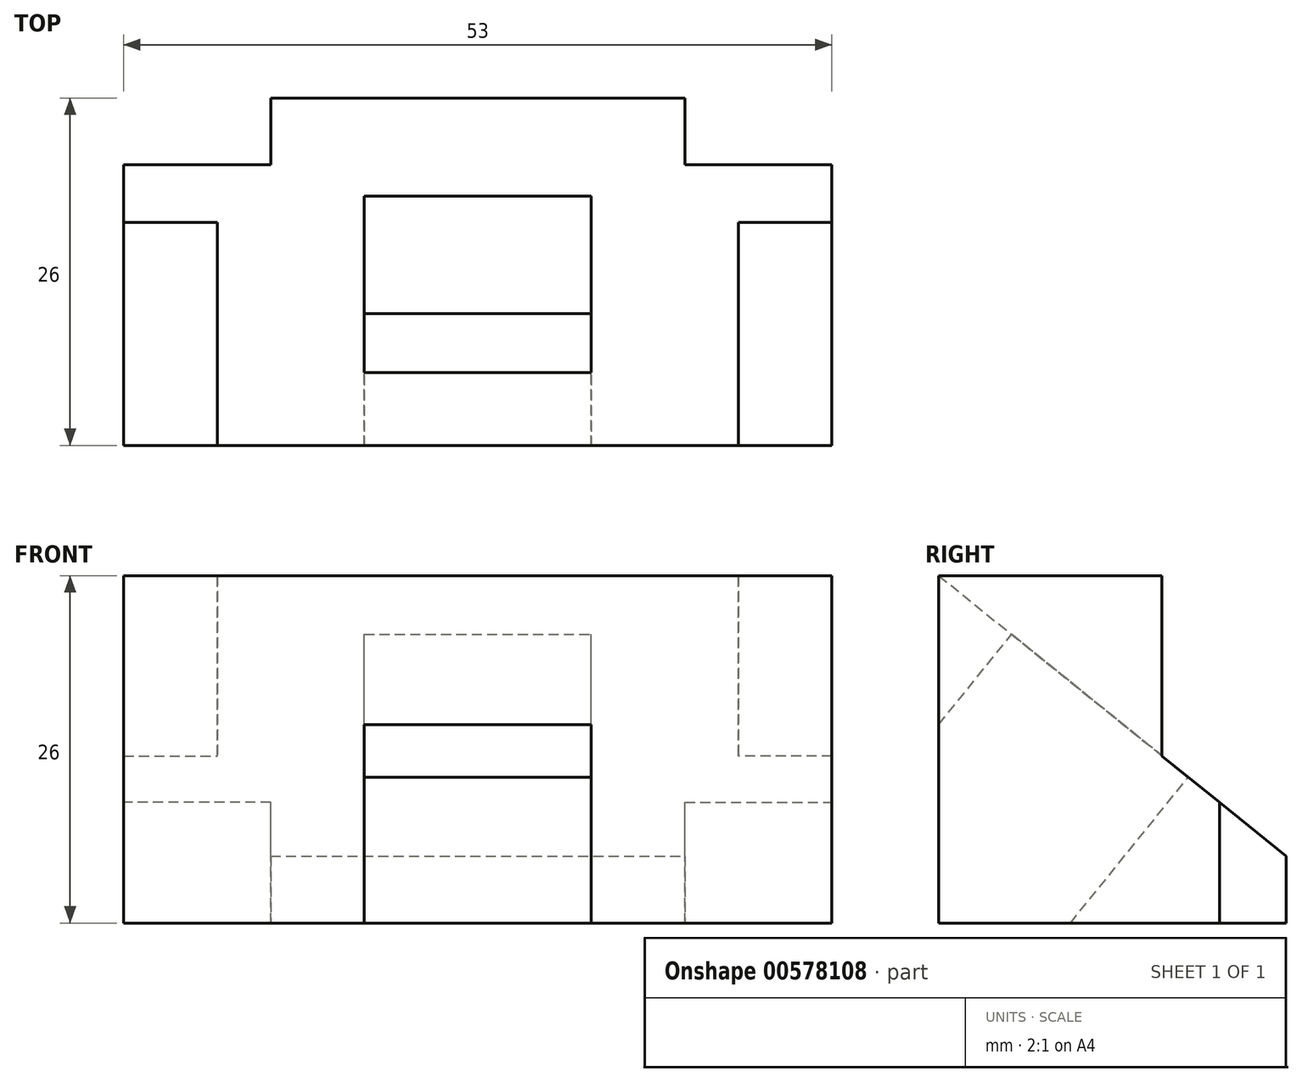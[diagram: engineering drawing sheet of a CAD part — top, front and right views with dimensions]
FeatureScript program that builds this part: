
annotation { "Feature Type Name" : "Feature", "Feature Type Description" : "" }
export const myFeature = defineFeature(function(context is Context, id is Id, definition is map)
    precondition{}
    {
        {
            var Q0;
            Q0=qCreatedBy(makeId("Top.planeOp"),FACE);
            var sketch = newSketch(context, id + "F0", { "sketchPlane" : qUnion([Q0])});
            skLineSegment(sketch, "E0.bottom", {"start": v(0, 0) * mm, "end": v(53, 0) * mm});
            skLineSegment(sketch, "E0.top", {"start": v(0, 26) * mm, "end": v(53, 26) * mm});
            skLineSegment(sketch, "E0.left", {"start": v(0, 0) * mm, "end": v(0, 26) * mm});
            skLineSegment(sketch, "E0.right", {"start": v(53, 0) * mm, "end": v(53, 26) * mm});
            skSolve(sketch);
        }
        {
            var Q0;
            Q0=makeQuery(id+"F0.imprint","IMPRINT",FACE,{"disambiguationData":[TD([[makeQuery(id+"F0.imprint","IMPRINT",EDGE,{"derivedFrom":sQuery(id+"F0.wireOp",EDGE,"E0.bottom")}),1.0]])]});
            extrude(context, id + "F1", {"entities" : qUnion([Q0]), "depth" : 26 * mm, "offsetDistance" : 25 * mm});
        }
        {
            var Q0;
            Q0=makeQuery(id+"F1.opExtrude","SWEPT_FACE",FACE,{"disambiguationData":[OSD([sQuery(id+"F0.wireOp",EDGE,"E0.right")])]});
            cPlane(context, id + "F2", {"entities" : qUnion([Q0]), "cplaneType" : CPlaneType.OFFSET, "offset" : 7 * mm, "oppositeDirection" : true, "width" : 150 * mm, "height" : 150 * mm});
        }
        {
            var Q0;
            Q0=qCreatedBy(id+"F2.planeOp",FACE);
            var sketch = newSketch(context, id + "F3", { "sketchPlane" : qUnion([Q0])});
            skLineSegment(sketch, "E1", {"start": v(0, 26) * mm, "end": v(26, 5) * mm});
            skLineSegment(sketch, "E2", {"start": v(26, 5) * mm, "end": v(26, 26) * mm});
            skLineSegment(sketch, "E3", {"start": v(26, 26) * mm, "end": v(0, 26) * mm});
            skSolve(sketch);
        }
        {
            var Q0;
            Q0 = qSketchRegion(id + "F3", true);
            extrude(context, id + "F4", {"entities" : qUnion([Q0]), "operationType" : NewBodyOperationType.REMOVE, "oppositeDirection" : true, "depth" : 39 * mm, "offsetDistance" : 25 * mm});
        }
        {
            var Q0;
            Q0=makeQuery(id+"F1.opExtrude","SWEPT_FACE",FACE,{"disambiguationData":[OSD([sQuery(id+"F0.wireOp",EDGE,"E0.right")])]});
            var sketch = newSketch(context, id + "F5", { "sketchPlane" : qUnion([Q0])});
            skLineSegment(sketch, "E4.bottom", {"start": v(26, 0) * mm, "end": v(21, 0) * mm});
            skLineSegment(sketch, "E4.top", {"start": v(26, 11) * mm, "end": v(21, 11) * mm});
            skLineSegment(sketch, "E4.left", {"start": v(26, 0) * mm, "end": v(26, 11) * mm});
            skLineSegment(sketch, "E4.right", {"start": v(21, 0) * mm, "end": v(21, 11) * mm});
            skSolve(sketch);
        }
        {
            var Q0;
            Q0 = qSketchRegion(id + "F5", true);
            extrude(context, id + "F6", {"entities" : qUnion([Q0]), "operationType" : NewBodyOperationType.REMOVE, "oppositeDirection" : true, "depth" : 11 * mm, "offsetDistance" : 25 * mm});
        }
        {
            var Q0;
            Q0=makeQuery(id+"F1.opExtrude","SWEPT_FACE",FACE,{"disambiguationData":[OSD([sQuery(id+"F0.wireOp",EDGE,"E0.right")])]});
            var sketch = newSketch(context, id + "F7", { "sketchPlane" : qUnion([Q0])});
            skLineSegment(sketch, "E5", {"start": v(16.7, 14) * mm, "end": v(16.7, 26) * mm});
            skLineSegment(sketch, "E6", {"start": v(16.7, 14) * mm, "end": v(25.18, 10.04) * mm});
            skSolve(sketch);
        }
        {
            var Q0;
            Q0 = qSketchRegion(id + "F7", true);
            var Q1;
            {var subQ3=sQuery(id+"F7.wireOp",EDGE,"E5");Q1=makeQuery(id+"F7.imprint","IMPRINT",FACE,{"disambiguationData":[TD([[makeQuery(id+"F7.imprint","IMPRINT",EDGE,{"derivedFrom":subQ3}),-1.0]])]});}
            extrude(context, id + "F8", {"entities" : qUnion([Q0, Q1]), "operationType" : NewBodyOperationType.REMOVE, "endBound" : BoundingType.THROUGH_ALL, "oppositeDirection" : true, "depth" : 25 * mm, "offsetDistance" : 25 * mm});
        }
        {
            var Q0;
            Q0=makeQuery(id+"F1.opExtrude","SWEPT_FACE",FACE,{"disambiguationData":[OSD([sQuery(id+"F0.wireOp",EDGE,"E0.right")])]});
            var sketch = newSketch(context, id + "F9", { "sketchPlane" : qUnion([Q0])});
            skLineSegment(sketch, "E7", {"start": v(21, 11) * mm, "end": v(21, 12) * mm});
            skSolve(sketch);
        }
        {
            var Q0;
            {var subQ0=sQuery(id+"F9.wireOp",EDGE,"E7");Q0=makeQuery(id+"F9.imprint","IMPRINT",FACE,{"disambiguationData":[TD([[makeQuery(id+"F9.imprint","IMPRINT",EDGE,{"derivedFrom":subQ0}),-1.0]])]});}
            extrude(context, id + "F10", {"entities" : qUnion([Q0]), "operationType" : NewBodyOperationType.REMOVE, "oppositeDirection" : true, "depth" : 18 * mm, "offsetDistance" : 25 * mm});
        }
        {
            var Q0;
            Q0=makeQuery(id+"F1.opExtrude","SWEPT_FACE",FACE,{"disambiguationData":[OSD([sQuery(id+"F0.wireOp",EDGE,"E0.right")])]});
            var sketch = newSketch(context, id + "F11", { "sketchPlane" : qUnion([Q0])});
            skLineSegment(sketch, "E8", {"start": v(21, 9.04) * mm, "end": v(16.7, 14) * mm});
            skSolve(sketch);
        }
        {
            var Q0;
            {var subQ0=sQuery(id+"F11.wireOp",EDGE,"E8");Q0=makeQuery(id+"F11.imprint","IMPRINT",FACE,{"disambiguationData":[TD([[makeQuery(id+"F11.imprint","IMPRINT",EDGE,{"derivedFrom":subQ0}),-1.0]])]});}
            extrude(context, id + "F12", {"entities" : qUnion([Q0]), "operationType" : NewBodyOperationType.REMOVE, "endBound" : BoundingType.THROUGH_ALL, "oppositeDirection" : true, "depth" : 25 * mm, "offsetDistance" : 25 * mm});
        }
        {
            var Q0;
            Q0=makeQuery(id+"F4.boolean.opBoolean","COPY",FACE,{"derivedFrom":makeQuery(id+"F4.opExtrude","CAP_FACE",FACE,{"disambiguationData":[OSD([sQuery(id+"F3.wireOp",EDGE,"E1"),sQuery(id+"F3.wireOp",EDGE,"E2"),sQuery(id+"F3.wireOp",EDGE,"E3")])],"isStart":true})});
            var sketch = newSketch(context, id + "F13", { "sketchPlane" : qUnion([Q0])});
            skLineSegment(sketch, "E9", {"start": v(-16.7, 14) * mm, "end": v(-16.7, 12.51) * mm});
            skSolve(sketch);
        }
        {
            var Q0;
            Q0 = qSketchRegion(id + "F13", true);
            var Q1;
            {var subQ0=sQuery(id+"F13.wireOp",EDGE,"E9");Q1=makeQuery(id+"F13.imprint","IMPRINT",FACE,{"disambiguationData":[TD([[makeQuery(id+"F13.imprint","IMPRINT",EDGE,{"derivedFrom":subQ0}),-1.0]])]});}
            extrude(context, id + "F14", {"entities" : qUnion([Q0, Q1]), "operationType" : NewBodyOperationType.REMOVE, "oppositeDirection" : true, "depth" : 25 * mm, "offsetDistance" : 25 * mm});
        }
        {
            var Q0;
            Q0=makeQuery(id+"F1.opExtrude","SWEPT_FACE",FACE,{"disambiguationData":[OSD([sQuery(id+"F0.wireOp",EDGE,"E0.left")])]});
            var sketch = newSketch(context, id + "F15", { "sketchPlane" : qUnion([Q0])});
            skLineSegment(sketch, "E10", {"start": v(-26, 5.5) * mm, "end": v(-21, 9.04) * mm});
            skLineSegment(sketch, "E11", {"start": v(-21, 9.04) * mm, "end": v(-21, 0) * mm});
            skLineSegment(sketch, "E12", {"start": v(-21, 0) * mm, "end": v(-26, 0) * mm});
            skLineSegment(sketch, "E13", {"start": v(-26, 0) * mm, "end": v(-26, 5.5) * mm});
            skSolve(sketch);
        }
        {
            var Q0;
            {var subQ4=sQuery(id+"F15.wireOp",EDGE,"E10");Q0=makeQuery(id+"F15.imprint","IMPRINT",FACE,{"disambiguationData":[TD([[makeQuery(id+"F15.imprint","IMPRINT",EDGE,{"derivedFrom":subQ4}),1.0]])]});}
            extrude(context, id + "F16", {"entities" : qUnion([Q0]), "operationType" : NewBodyOperationType.REMOVE, "oppositeDirection" : true, "depth" : 25 * mm, "offsetDistance" : 25 * mm});
        }
        {
            var Q0;
            Q0=makeQuery(id+"F4.boolean.opBoolean","COPY",FACE,{"derivedFrom":makeQuery(id+"F4.opExtrude","CAP_FACE",FACE,{"disambiguationData":[OSD([sQuery(id+"F3.wireOp",EDGE,"E1"),sQuery(id+"F3.wireOp",EDGE,"E2"),sQuery(id+"F3.wireOp",EDGE,"E3")])],"isStart":false})});
            var sketch = newSketch(context, id + "F17", { "sketchPlane" : qUnion([Q0])});
            skLineSegment(sketch, "E14", {"start": v(16.7, 14) * mm, "end": v(16.7, 12.51) * mm});
            skSolve(sketch);
        }
        {
            var Q0;
            Q0 = qSketchRegion(id + "F17", true);
            var Q1;
            {var subQ4=sQuery(id+"F17.wireOp",EDGE,"E14");Q1=makeQuery(id+"F17.imprint","IMPRINT",FACE,{"disambiguationData":[TD([[makeQuery(id+"F17.imprint","IMPRINT",EDGE,{"derivedFrom":subQ4}),1.0]])]});}
            extrude(context, id + "F18", {"entities" : qUnion([Q0, Q1]), "operationType" : NewBodyOperationType.REMOVE, "endBound" : BoundingType.THROUGH_ALL, "oppositeDirection" : true, "depth" : 25 * mm, "offsetDistance" : 25 * mm});
        }
        {
            var Q0;
            Q0=makeQuery(id+"F1.opExtrude","SWEPT_FACE",FACE,{"disambiguationData":[OSD([sQuery(id+"F0.wireOp",EDGE,"E0.left")])]});
            var sketch = newSketch(context, id + "F19", { "sketchPlane" : qUnion([Q0])});
            skLineSegment(sketch, "E15", {"start": v(-21, 0) * mm, "end": v(-21, 9.04) * mm});
            skSolve(sketch);
        }
        {
            var Q0;
            {var subQ0=sQuery(id+"F19.wireOp",EDGE,"E15");Q0=makeQuery(id+"F19.imprint","IMPRINT",FACE,{"disambiguationData":[TD([[makeQuery(id+"F19.imprint","IMPRINT",EDGE,{"derivedFrom":subQ0}),1.0]])]});}
            extrude(context, id + "F20", {"entities" : qUnion([Q0]), "operationType" : NewBodyOperationType.REMOVE, "oppositeDirection" : true, "depth" : 11 * mm, "offsetDistance" : 25 * mm});
        }
        {
            var Q0;
            {var subQ0=sQuery(id+"F3.wireOp",EDGE,"E1");Q0=makeQuery(id+"F18.boolean.opBoolean","MERGE",FACE,{"derivedFrom":[makeQuery(id+"F14.boolean.opBoolean","MERGE",FACE,{"derivedFrom":[makeQuery(id+"F4.boolean.opBoolean","COPY",FACE,{"derivedFrom":makeQuery(id+"F4.opExtrude","SWEPT_FACE",FACE,{"disambiguationData":[OSD([subQ0])]})}),makeQuery(id+"F14.opExtrude","SWEPT_FACE",FACE,{"disambiguationData":[OSD([subQ0])]})]}),makeQuery(id+"F18.opExtrude","SWEPT_FACE",FACE,{"disambiguationData":[OSD([subQ0])]})]});}
            var sketch = newSketch(context, id + "F21", { "sketchPlane" : qUnion([Q0])});
            skLineSegment(sketch, "E16", {"start": v(18, 7.66) * mm, "end": v(18, -9.34) * mm});
            skLineSegment(sketch, "E17", {"start": v(18, -9.34) * mm, "end": v(35, -9.34) * mm});
            skLineSegment(sketch, "E18", {"start": v(18, 7.66) * mm, "end": v(35, 7.66) * mm});
            skLineSegment(sketch, "E19", {"start": v(35, 7.66) * mm, "end": v(35, -9.34) * mm});
            skSolve(sketch);
        }
        {
            var Q0;
            Q0=makeQuery(id+"F21.imprint","IMPRINT",FACE,{"disambiguationData":[TD([[makeQuery(id+"F21.imprint","IMPRINT",EDGE,{"derivedFrom":sQuery(id+"F21.wireOp",EDGE,"E16")}),1.0]])]});
            extrude(context, id + "F22", {"entities" : qUnion([Q0]), "operationType" : NewBodyOperationType.REMOVE, "endBound" : BoundingType.THROUGH_ALL, "oppositeDirection" : true, "depth" : 25 * mm, "offsetDistance" : 25 * mm});
        }
    });
